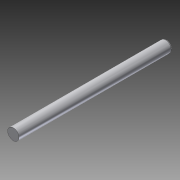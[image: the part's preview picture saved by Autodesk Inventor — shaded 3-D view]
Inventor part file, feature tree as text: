
AUTODESK INVENTOR PART (.ipt)
format: ipt  version: 2015 (Build 190159000, 159)  size: 82,944 bytes
history: native  units: mm
features: fillet x2, extrude x1, hole x1, sketch x1
ambient origin geometry x8: Origin, YZ Plane, XZ Plane, XY Plane, X Axis, Y Axis, Z Axis, Center Point
bodies: Solid1 (feature_tree)
feature tree (5):
  extrude  "Extrusion1"  Depth=68.0mm TaperAngle=0.0deg
  fillet  "Fillet1"  Radius=0.5mm
  hole  "Hole1"  [1 undecoded]
  fillet  "Fillet2"  Radius=0.25mm
  sketch  "Sketch1"  dims[d0=5.0mm d1=68.0mm d2=0.0mm d3=0.5mm d4=10.0mm d5=10.0mm d6=2.0mm d7=6.0mm d8=4.0mm d9=2.0mm d10=90.0deg d11=10.0mm d12=0.0mm d13=0.25mm]
note: 1 required parameter value undecoded (feature->parameter linkage not recoverable at this tier; creation-order binding heuristic only, values carry confidence <= 0.55)
